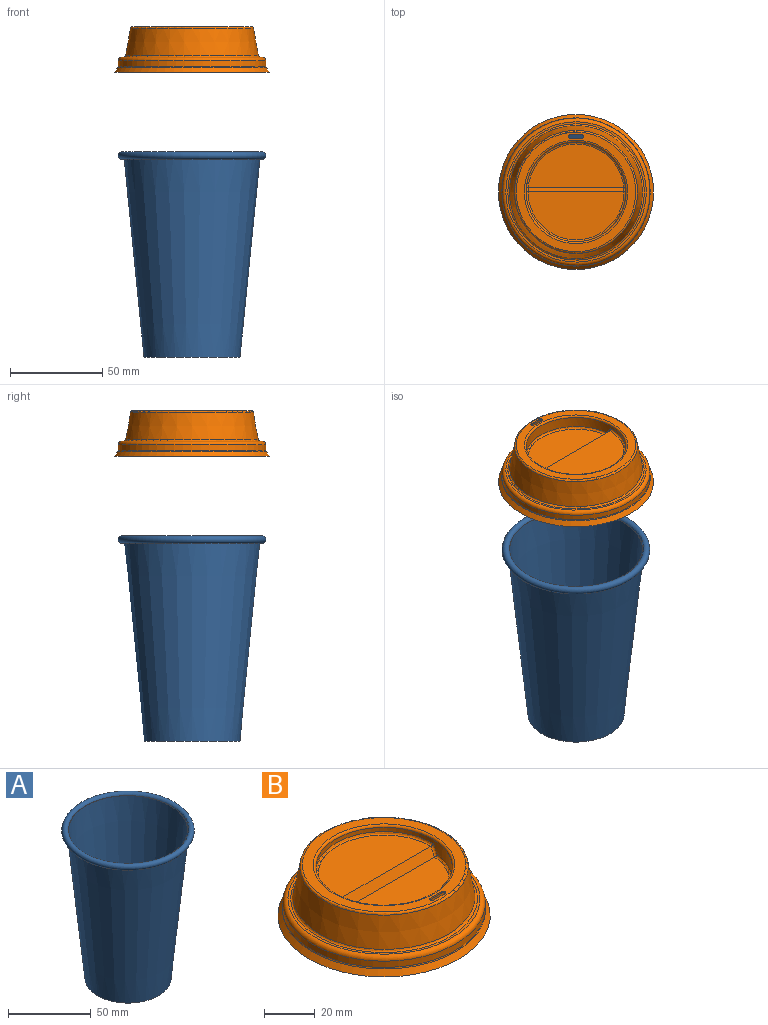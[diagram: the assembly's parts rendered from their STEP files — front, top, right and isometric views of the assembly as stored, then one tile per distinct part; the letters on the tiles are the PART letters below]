
ASSEMBLY  parts=2 mates=1
PART A: 8 faces, bbox 86.5x86.5x109.5 mm
  f0: cone r=25mm half-angle=5.7deg, axis (0,0,1), area 20121.4mm2, adj f1,f6
  f1: cone r=36mm half-angle=84.3deg, axis (0,0,-1), area 3.1mm2, adj f0,f5
  f2: cone r=25.99mm half-angle=5.7deg, axis (0,0,1), area 21326.5mm2, adj f3,f5
  f3: cone r=25mm half-angle=84.3deg, axis (0,0,-1), area 160.2mm2, adj f2,f4
  f4: cone r=25mm half-angle=5.7deg, axis (0,0,1), area 797.3mm2, adj f3,f7
  f5: torus R=37.98mm, axis (0,0,1), area 2483.9mm2, adj f1,f2
  f6: plane 51.21x51.21mm, normal (0,0,1), area 2059.4mm2, adj f0
  f7: plane 51.01x51.01mm, normal (0,0,-1), area 2043.2mm2, adj f4
PART B: 45 faces, bbox 87.2x87.2x24.8 mm
  f0: plane 52x26.11mm, normal (0,0,1), area 1067.4mm2, adj f14,f15,f16,f18
  f1: plane 84x84mm, normal (0,0,-1), area 254.4mm2, adj f2,f20
  f2: cone r=40mm half-angle=34.9deg, axis (0,0,-1), area 821.4mm2, adj f1,f10
  f3: cylinder r=40mm len=80mm, axis (0,0,1), area 758.6mm2, adj f10,f12
  f4: plane 76x76mm, normal (0,0,1), area 254.1mm2, adj f11,f12
  f5: cone r=33.18mm half-angle=10deg, axis (0,0,-1), area 3266mm2, adj f8,f11
  f6: plane 64.69x64.69mm, normal (0,0,1), area 808.2mm2, adj f8,f9,f37,f38,f39,f40,f41,f42
  f7: cylinder r=27mm len=54mm, axis (0,0,1), area 663.3mm2, adj f9,f15,f16,f17,f18
  f8: torus R=32.34mm, axis (0,0,1), area 289mm2, adj f5,f6
  f9: torus R=28mm, axis (0,0,1), area 270.1mm2, adj f6,f7
  f10: torus R=41mm, axis (0,0,1), area 153.3mm2, adj f2,f3
  f11: torus R=36.92mm, axis (0,0,1), area 318.7mm2, adj f4,f5
  f12: torus R=38mm, axis (0,0,1), area 775.2mm2, adj f3,f4
  f13: plane 51.78x23.59mm, normal (0,0,1), area 936.4mm2, adj f14,f15,f17,f18
  f14: plane 51.96x4mm, normal (0,-0.87,0.5), area 239.3mm2, adj f0,f13,f15,f18
  f15: bspline ~10.37x6.71mm, area 7.6mm2, adj f0,f7,f13,f14,f16,f17
  f16: torus R=26mm, axis (0,0,1), area 132.7mm2, adj f0,f7,f15,f18
  f17: torus R=26mm, axis (0,0,1), area 122.7mm2, adj f7,f13,f15,f18
  f18: bspline ~10.37x6.71mm, area 7.6mm2, adj f0,f7,f13,f14,f16,f17
  f19: plane 52x25.65mm, normal (0,0,-1), area 1043.4mm2, adj f32,f33,f34,f36
  f20: cone r=39.34mm half-angle=34.9deg, axis (0,0,-1), area 663.9mm2, adj f1,f28
  f21: cylinder r=39.2mm len=78.4mm, axis (0,0,1), area 743.4mm2, adj f28,f30
  f22: plane 76x76mm, normal (0,0,-1), area 254.1mm2, adj f29,f30
  f23: cone r=32.4mm half-angle=10deg, axis (0,0,-1), area 3191.7mm2, adj f26,f29
  f24: plane 64.69x64.69mm, normal (0,0,-1), area 808.2mm2, adj f26,f27,f37,f38,f39,f40,f41,f42
  f25: cylinder r=27.8mm len=55.6mm, axis (0,0,1), area 682.9mm2, adj f27,f33,f34,f35,f36
  f26: torus R=32.34mm, axis (0,0,1), area 57mm2, adj f23,f24
  f27: torus R=28mm, axis (0,0,1), area 55mm2, adj f24,f25
  f28: torus R=41mm, axis (0,0,1), area 270.8mm2, adj f20,f21
  f29: torus R=36.92mm, axis (0,0,1), area 566.2mm2, adj f22,f23
  f30: torus R=38mm, axis (0,0,1), area 459.1mm2, adj f21,f22
  f31: plane 51.85x24.05mm, normal (0,0,-1), area 960.3mm2, adj f32,f33,f35,f36
  f32: plane 51.94x4mm, normal (0,0.87,-0.5), area 239.1mm2, adj f19,f31,f33,f36
  f33: bspline ~16.72x11.09mm, area 13.9mm2, adj f19,f25,f31,f32,f34,f35
  f34: torus R=26mm, axis (0,0,1), area 242.1mm2, adj f19,f25,f33,f36
  f35: torus R=26mm, axis (0,0,1), area 226.4mm2, adj f25,f31,f33,f36
  f36: bspline ~16.72x11.09mm, area 13.9mm2, adj f19,f25,f31,f32,f34,f35
  f37: plane 0.8x0.4mm, normal (1,0,0), area 0.3mm2, adj f6,f24,f38,f44
  f38: cylinder r=0.8mm len=0.8mm, axis (0,0,1), area 1mm2, adj f6,f24,f37,f39
  f39: plane 6.4x0.8mm, normal (0,1,0), area 5.1mm2, adj f6,f24,f38,f40
  f40: cylinder r=0.8mm len=0.8mm, axis (0,0,1), area 1mm2, adj f6,f24,f39,f41
  f41: plane 0.8x0.4mm, normal (-1,0,0), area 0.3mm2, adj f6,f24,f40,f42
  f42: cylinder r=0.8mm len=0.8mm, axis (0,0,1), area 1mm2, adj f6,f24,f41,f43
  f43: plane 6.4x0.8mm, normal (0,-1,0), area 5.1mm2, adj f6,f24,f42,f44
  f44: cylinder r=0.8mm len=0.8mm, axis (0,0,1), area 1mm2, adj f6,f24,f37,f43
PLACE A t=(0,0,10.2)mm fixed
PLACE B rot(axis=(0,0,1),180deg) t=(0,0,61.16)mm
MATE cylindrical B.f2 <-> A.f0  axis (0,0,1) through (0,0,137.02)mm
